# Revit family: Electrical-Box_FSR_FL640P
name_source: partatom
category: Electrical Fixtures
units: mm (PartAtom-declared; Revit-internal decimal feet)

## family parameters
Cut with Voids When Loaded = No
Host = Face
Maintain Annotation Orientation = No
Part Type = Normal
Room Calculation Point = No
Round Connector Dimension = Use Diameter
Shared = No

## types (6) — shared parameters
Apparent Load = 0 VA
Assembly Code = D5020100
Body Material = Material and Finish as Specified in 26 27 26
Building Codes = ftp://doclib.fsrinc.com/
Connections = 1" - 1 1/4" Knockouts
Construction Details = ftp://doclib.fsrinc.com/
Default Elevation = 48 "
Green Building-LEED = http://www.arcat.com
Installation-Fabrication = ftp://doclib.fsrinc.com/
Keynote = 26 27 26
Manufacturer = FSR Inc.
Manufacturer Fax = 973-785-4207
Manufacturer Website = http://www.fsrinc.com
Model = FL-640P
Pole = 1
Product Data = http://www.arcat.com
Sales Information = http://www.fsrinc.com
Send Message = http://admin.arcat.com
Specification = http://www.arcat.com
Test Data = ftp://doclib.fsrinc.com/
URL = http://www.fsrinc.com
zero-valued in all types: Expected Lifespan (Years), Maintenance Schedule (Months), Warranty Duration (Years)

## per-type parameters (varying)
| type | Cover Material | Description | Voltage |
| 6" Height - 1/4" Edging - Brass Cover | Brass | FSR FL-640P - 6" Height - 1/4" Edging - Brass Cover | 0 V |
| 6" Height - 1/4" Edging - Black Cover | Black | FSR FL-640P - 6" Height - 1/4" Edging - Black Cover | 0 V |
| 6" Height - 1/4" Edging - Gray Cover | Gray | FSR FL-640P - 6" Height - 1/4" Edging - Gray Cover | 0 V |
| 4" Height - 1/4" Edging - Gray Cover | Gray | FSR FL-640P - 4" Height - 1/4" Edging - Gray Cover | 120 V |
| 4" Height - 1/4" Edging - Brass Cover | Brass | FSR FL-640P - 4" Height - 1/4" Edging - Brass Cover | 0 V |
| 4" Height - 1/4" Edging - Black Cover | Black | FSR FL-640P - 4" Height - 1/4" Edging - Black Cover | 0 V |

## geometry (parser evidence)
native form markers: Sweep x3
no freeform markers — native parametric forms only
